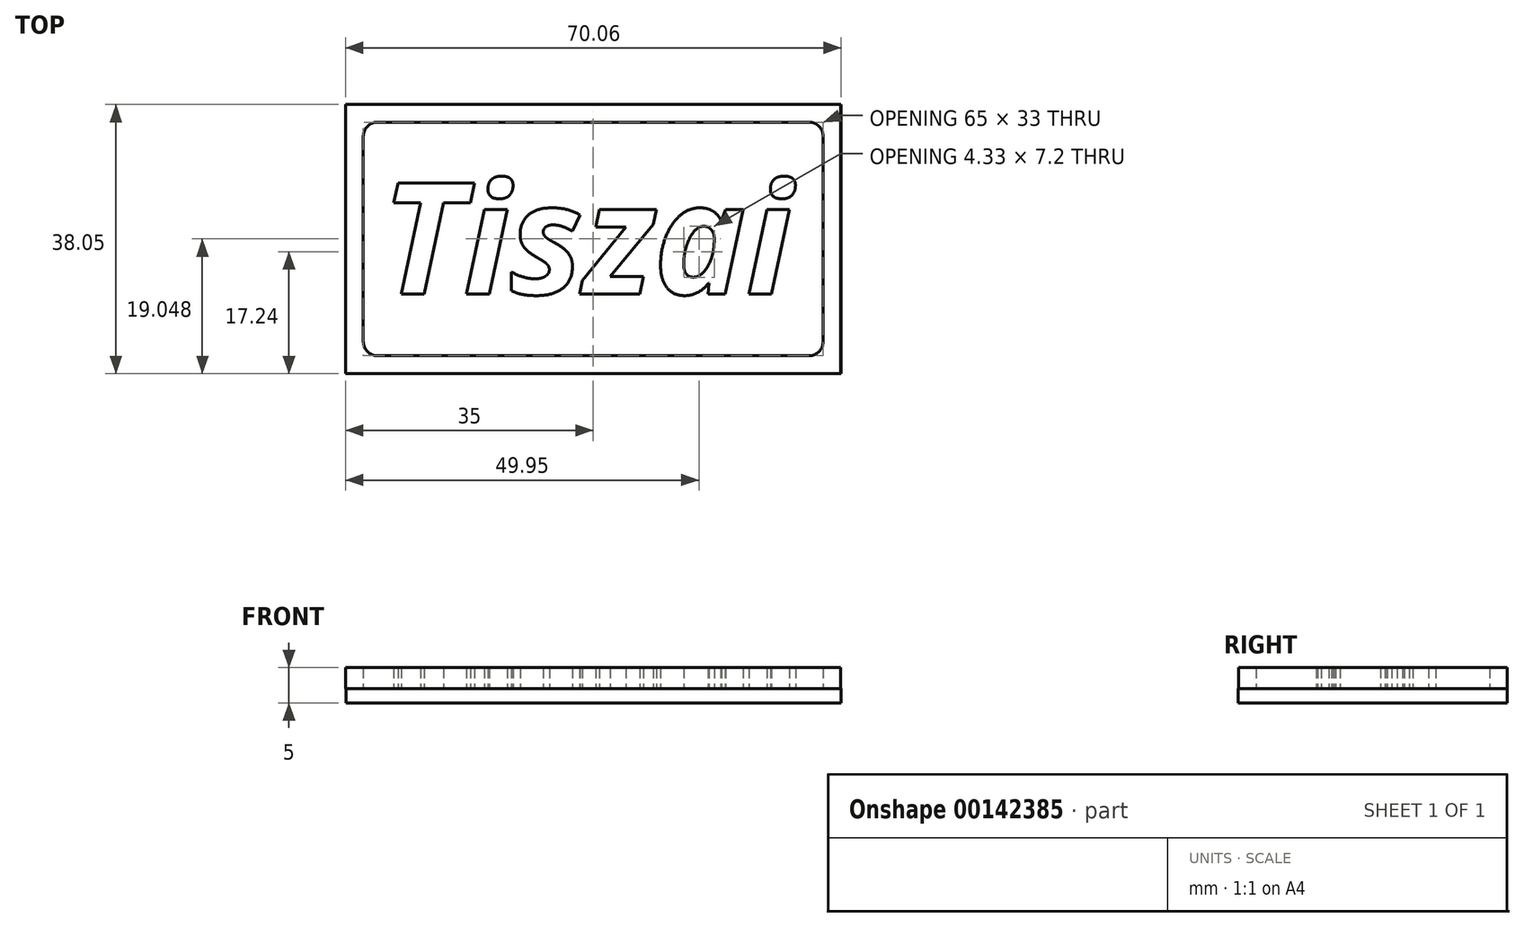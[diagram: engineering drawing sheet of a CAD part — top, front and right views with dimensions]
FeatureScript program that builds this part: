
annotation { "Feature Type Name" : "Feature", "Feature Type Description" : "" }
export const myFeature = defineFeature(function(context is Context, id is Id, definition is map)
    precondition{}
    {
        {
            var Q0;
            Q0=qCreatedBy(makeId("Top.planeOp"),FACE);
            var sketch = newSketch(context, id + "F0", { "sketchPlane" : qUnion([Q0])});
            skLineSegment(sketch, "E0.bottom", {"start": v(-34.27, 17.47) * mm, "end": v(35.73, 17.47) * mm});
            skLineSegment(sketch, "E0.top", {"start": v(-34.27, -20.53) * mm, "end": v(35.73, -20.53) * mm});
            skLineSegment(sketch, "E0.left", {"start": v(-34.27, 17.47) * mm, "end": v(-34.27, -20.53) * mm});
            skLineSegment(sketch, "E0.right", {"start": v(35.73, 17.47) * mm, "end": v(35.73, -20.53) * mm});
            skLineSegment(sketch, "E1.0", {"start": v(-29.77, 14.97) * mm, "end": v(31.23, 14.97) * mm});
            skLineSegment(sketch, "E1.1", {"start": v(-31.77, 12.97) * mm, "end": v(-31.77, -16.03) * mm});
            skLineSegment(sketch, "E1.2", {"start": v(-29.77, -18.03) * mm, "end": v(31.23, -18.03) * mm});
            skLineSegment(sketch, "E1.3", {"start": v(33.23, 12.97) * mm, "end": v(33.23, -16.03) * mm});
            skText(sketch, "E2", { "text": "Tiszai", "fontName": "OpenSans-BoldItalic.ttf"});
            skPoint(sketch, "E3.visualSharp", {"position": v(-31.77, 14.97) * mm});
            skArc(sketch, "E3.filletArc", {"start": v(-29.77, 14.97) * mm, "mid": v(-31.18, 14.38) * mm, "end": v(-31.77, 12.97) * mm});
            skPoint(sketch, "E4.visualSharp", {"position": v(-31.77, -18.03) * mm});
            skArc(sketch, "E4.filletArc", {"start": v(-31.77, -16.03) * mm, "mid": v(-31.18, -17.45) * mm, "end": v(-29.77, -18.03) * mm});
            skPoint(sketch, "E5.visualSharp", {"position": v(33.23, -18.03) * mm});
            skArc(sketch, "E5.filletArc", {"start": v(31.23, -18.03) * mm, "mid": v(32.64, -17.45) * mm, "end": v(33.23, -16.03) * mm});
            skPoint(sketch, "E6.visualSharp", {"position": v(33.23, 14.97) * mm});
            skArc(sketch, "E6.filletArc", {"start": v(33.23, 12.97) * mm, "mid": v(32.64, 14.38) * mm, "end": v(31.23, 14.97) * mm});
            const initialGuessF0  = {"E2": [-0.02925, -0.00933, 1, 0, 0.0158]};
            skSetInitialGuess(sketch, initialGuessF0);
            skSolve(sketch);
        }
        {
            var Q0;
            Q0=makeQuery(id+"F0.imprint","IMPRINT",FACE,{"disambiguationData":[TD([[makeQuery(id+"F0.imprint","IMPRINT",EDGE,{"derivedFrom":sQuery(id+"F0.wireOp",EDGE,"E2.sketch_text.stroke-19")}),-1.0]])]});
            var Q1;
            Q1=makeQuery(id+"F0.imprint","IMPRINT",FACE,{"disambiguationData":[TD([[makeQuery(id+"F0.imprint","IMPRINT",EDGE,{"derivedFrom":sQuery(id+"F0.wireOp",EDGE,"E2.sketch_text.stroke-15")}),-1.0]])]});
            var Q2;
            Q2=makeQuery(id+"F0.imprint","IMPRINT",FACE,{"disambiguationData":[TD([[makeQuery(id+"F0.imprint","IMPRINT",EDGE,{"derivedFrom":sQuery(id+"F0.wireOp",EDGE,"E2.sketch_text.stroke-0")}),-1.0]])]});
            var Q3;
            Q3=makeQuery(id+"F0.imprint","IMPRINT",FACE,{"disambiguationData":[TD([[makeQuery(id+"F0.imprint","IMPRINT",EDGE,{"derivedFrom":sQuery(id+"F0.wireOp",EDGE,"E2.sketch_text.stroke-42")}),-1.0]])]});
            var Q4;
            Q4=makeQuery(id+"F0.imprint","IMPRINT",FACE,{"disambiguationData":[TD([[makeQuery(id+"F0.imprint","IMPRINT",EDGE,{"derivedFrom":sQuery(id+"F0.wireOp",EDGE,"E2.sketch_text.stroke-52")}),-1.0]])]});
            var Q5;
            Q5=makeQuery(id+"F0.imprint","IMPRINT",FACE,{"disambiguationData":[TD([[makeQuery(id+"F0.imprint","IMPRINT",EDGE,{"derivedFrom":sQuery(id+"F0.wireOp",EDGE,"E2.sketch_text.stroke-84")}),-1.0]])]});
            var Q6;
            Q6=makeQuery(id+"F0.imprint","IMPRINT",FACE,{"disambiguationData":[TD([[makeQuery(id+"F0.imprint","IMPRINT",EDGE,{"derivedFrom":sQuery(id+"F0.wireOp",EDGE,"E2.sketch_text.stroke-8")}),-1.0]])]});
            var Q7;
            Q7=makeQuery(id+"F0.imprint","IMPRINT",FACE,{"disambiguationData":[TD([[makeQuery(id+"F0.imprint","IMPRINT",EDGE,{"derivedFrom":sQuery(id+"F0.wireOp",EDGE,"E2.sketch_text.stroke-77")}),-1.0]])]});
            extrude(context, id + "F1", {"entities" : qUnion([Q0, Q1, Q2, Q3, Q4, Q5, Q6, Q7]), "depth" : 3 * mm});
        }
        {
            var Q0;
            Q0 = qSketchRegion(id + "F0", true);
            extrude(context, id + "F2", {"entities" : qUnion([Q0]), "depth" : 3 * mm});
        }
        {
            var Q0;
            Q0=qCreatedBy(makeId("Top.planeOp"),FACE);
            var sketch = newSketch(context, id + "F3", { "sketchPlane" : qUnion([Q0])});
            skLineSegment(sketch, "E7.bottom", {"start": v(-34.21, 17.42) * mm, "end": v(35.79, 17.42) * mm});
            skLineSegment(sketch, "E7.top", {"start": v(-34.21, -20.58) * mm, "end": v(35.79, -20.58) * mm});
            skLineSegment(sketch, "E7.left", {"start": v(-34.21, 17.42) * mm, "end": v(-34.21, -20.58) * mm});
            skLineSegment(sketch, "E7.right", {"start": v(35.79, 17.42) * mm, "end": v(35.79, -20.58) * mm});
            skSolve(sketch);
        }
        {
            var Q0;
            Q0 = qSketchRegion(id + "F3", true);
            extrude(context, id + "F4", {"entities" : qUnion([Q0]), "oppositeDirection" : true, "depth" : 2 * mm});
        }
    });
